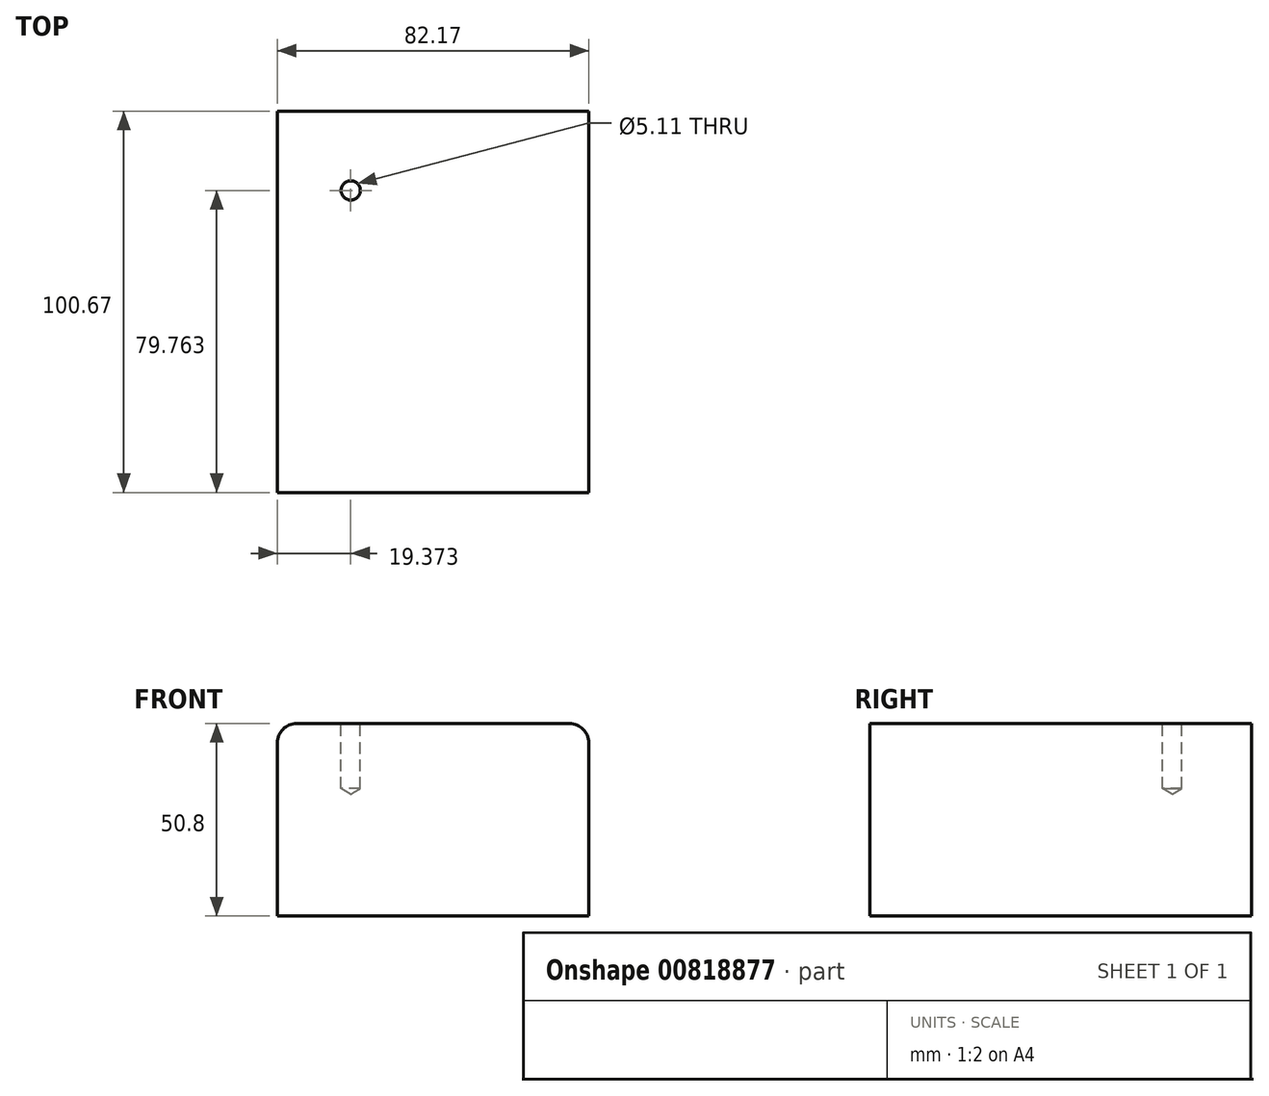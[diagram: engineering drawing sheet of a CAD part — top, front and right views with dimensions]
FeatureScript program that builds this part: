
annotation { "Feature Type Name" : "Feature", "Feature Type Description" : "" }
export const myFeature = defineFeature(function(context is Context, id is Id, definition is map)
    precondition{}
    {
        {
            var Q0;
            Q0=qCreatedBy(makeId("Top.planeOp"),FACE);
            var sketch = newSketch(context, id + "F0", { "sketchPlane" : qUnion([Q0])});
            skLineSegment(sketch, "E0.bottom", {"start": v(-36.19, 52.51) * mm, "end": v(45.98, 52.51) * mm});
            skLineSegment(sketch, "E0.top", {"start": v(-36.19, -48.16) * mm, "end": v(45.98, -48.16) * mm});
            skLineSegment(sketch, "E0.left", {"start": v(-36.19, 52.51) * mm, "end": v(-36.19, -48.16) * mm});
            skLineSegment(sketch, "E0.right", {"start": v(45.98, 52.51) * mm, "end": v(45.98, -48.16) * mm});
            skSolve(sketch);
        }
        {
            var Q0;
            Q0 = qSketchRegion(id + "F0", true);
            extrude(context, id + "F1", {"entities" : qUnion([Q0]), "depth" : 50.8 * mm, "offsetDistance" : 25.4 * mm});
        }
        {
            var Q0;
            Q0=makeQuery(id+"F1.opExtrude","CAP_FACE",FACE,{"disambiguationData":[OSD([sQuery(id+"F0.wireOp",EDGE,"E0.bottom"),sQuery(id+"F0.wireOp",EDGE,"E0.top"),sQuery(id+"F0.wireOp",EDGE,"E0.left"),sQuery(id+"F0.wireOp",EDGE,"E0.right")])],"isStart":false});
            var sketch = newSketch(context, id + "F2", { "sketchPlane" : qUnion([Q0])});
            skPoint(sketch, "E1", {"position": v(-16.82, 31.6) * mm});
            skSolve(sketch);
        }
        {
            var Q0;
            Q0=sQuery(id+"F2.wireOp",VERTEX,"E1");
            var Q1;
            Q1=makeQuery(id+"F1.opExtrude","SWEPT_BODY",BODY,{"disambiguationData":[OSD([sQuery(id+"F0.wireOp",EDGE,"E0.bottom"),sQuery(id+"F0.wireOp",EDGE,"E0.top"),sQuery(id+"F0.wireOp",EDGE,"E0.left"),sQuery(id+"F0.wireOp",EDGE,"E0.right")])]});
            hole(context, id + "F3", {"style" : HoleStyle.SIMPLE, "endStyle" : HoleEndStyle.BLIND, "standardTappedOrClearance" : lookupTablePath({ "standard" : "ANSI", "engagement" : "75%", "pitch" : "20 tpi", "size" : "1/4", "type" : "Tapped" }), "standardBlindInLast" : lookupTablePath({ "standard" : "ANSI", "engagement" : "75%", "pitch" : "20 tpi", "size" : "1/4", "type" : "Tapped" }), "holeDiameter" : 5.1 * mm, "majorDiameter" : 6.35 * mm, "showTappedDepth" : true, "holeDepth" : 17.14 * mm, "isTappedThrough" : true, "tappedDepth" : 12.7 * mm, "tapClearance" : 3.5, "locations" : qUnion([Q0]), "scope" : qUnion([Q1])});
        }
        {
            var Q0;
            Q0=makeQuery(id+"F1.opExtrude","CAP_EDGE",EDGE,{"disambiguationData":[OSD([sQuery(id+"F0.wireOp",EDGE,"E0.right")])],"isStart":false});
            var Q1;
            Q1=makeQuery(id+"F1.opExtrude","CAP_EDGE",EDGE,{"disambiguationData":[OSD([sQuery(id+"F0.wireOp",EDGE,"E0.left")])],"isStart":false});
            fillet(context, id + "F4", {"entities" : qUnion([Q0, Q1]), "radius" : 5.08 * mm, "tangentPropagation" : true, "allowEdgeOverflow" : false});
        }
    });
